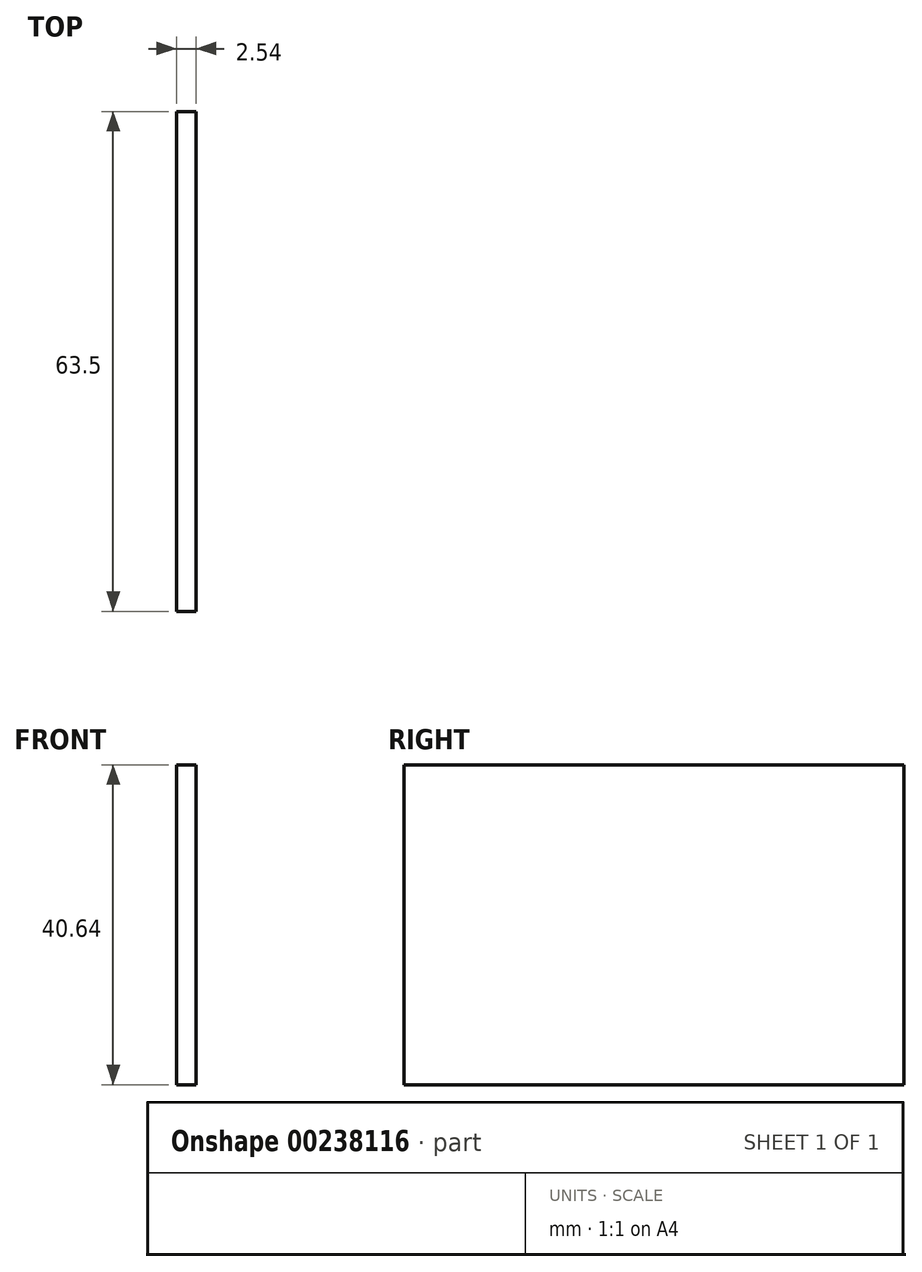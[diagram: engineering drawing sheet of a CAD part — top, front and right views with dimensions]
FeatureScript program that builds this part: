
annotation { "Feature Type Name" : "Feature", "Feature Type Description" : "" }
export const myFeature = defineFeature(function(context is Context, id is Id, definition is map)
    precondition{}
    {
        {
            var Q0;
            Q0=qCreatedBy(makeId("Right.planeOp"),FACE);
            var sketch = newSketch(context, id + "F0", { "sketchPlane" : qUnion([Q0])});
            skLineSegment(sketch, "E0.bottom", {"start": v(-29.07, -8.24) * mm, "end": v(34.43, -8.24) * mm});
            skLineSegment(sketch, "E0.top", {"start": v(-29.07, 32.4) * mm, "end": v(34.43, 32.4) * mm});
            skLineSegment(sketch, "E0.left", {"start": v(-29.07, -8.24) * mm, "end": v(-29.07, 32.4) * mm});
            skLineSegment(sketch, "E0.right", {"start": v(34.43, -8.24) * mm, "end": v(34.43, 32.4) * mm});
            skSolve(sketch);
        }
        {
            var Q0;
            Q0=makeQuery(id+"F0.imprint","IMPRINT",FACE,{"disambiguationData":[TD([[makeQuery(id+"F0.imprint","IMPRINT",EDGE,{"derivedFrom":sQuery(id+"F0.wireOp",EDGE,"E0.bottom")}),1.0]])]});
            extrude(context, id + "F1", {"entities" : qUnion([Q0]), "depth" : 2.54 * mm});
        }
    });
